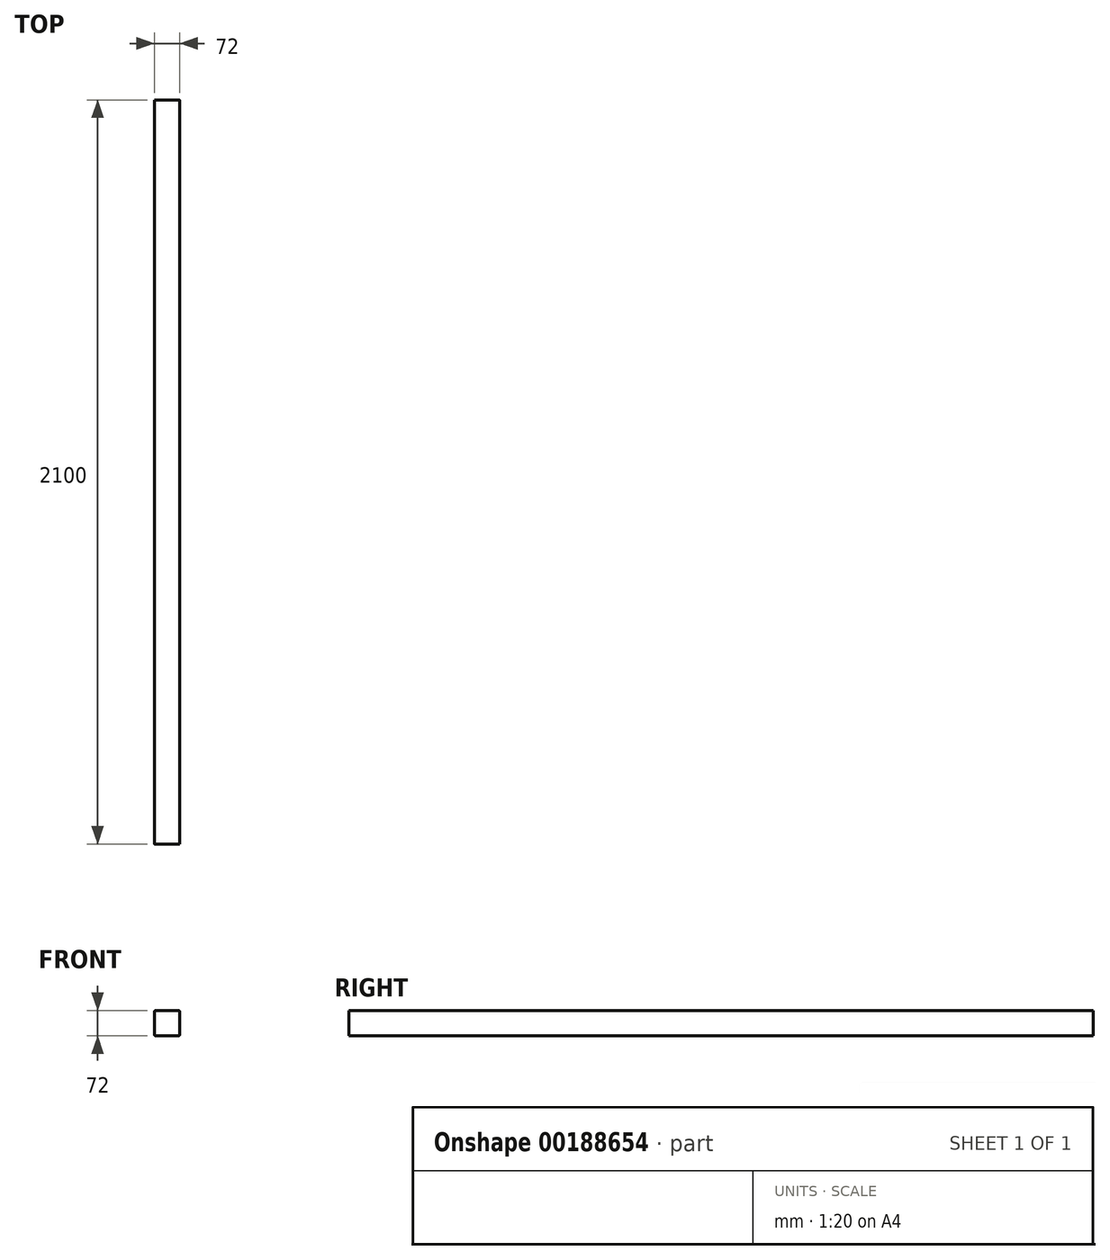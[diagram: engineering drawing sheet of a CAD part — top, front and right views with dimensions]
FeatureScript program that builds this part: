
annotation { "Feature Type Name" : "Feature", "Feature Type Description" : "" }
export const myFeature = defineFeature(function(context is Context, id is Id, definition is map)
    precondition{}
    {
        {
            var Q0;
            Q0=qCreatedBy(makeId("Front.planeOp"),FACE);
            var sketch = newSketch(context, id + "F0", { "sketchPlane" : qUnion([Q0])});
            skLineSegment(sketch, "E0.bottom", {"start": v(-31, 36) * mm, "end": v(31, 36) * mm});
            skLineSegment(sketch, "E0.top", {"start": v(-31, -36) * mm, "end": v(31, -36) * mm});
            skLineSegment(sketch, "E0.left", {"start": v(-36, 31) * mm, "end": v(-36, -31) * mm});
            skLineSegment(sketch, "E0.right", {"start": v(36, 31) * mm, "end": v(36, -31) * mm});
            skLineSegment(sketch, "E1", {"start": v(0, 53.32) * mm, "end": v(0, -69.02) * mm, "construction": true});
            skLineSegment(sketch, "E2", {"start": v(-62.16, 0) * mm, "end": v(68.96, 0) * mm, "construction": true});
            skPoint(sketch, "E3.visualSharp", {"position": v(-36, 36) * mm});
            skArc(sketch, "E3.filletArc", {"start": v(-31, 36) * mm, "mid": v(-34.54, 34.54) * mm, "end": v(-36, 31) * mm});
            skPoint(sketch, "E4.visualSharp", {"position": v(36, 36) * mm});
            skArc(sketch, "E4.filletArc", {"start": v(36, 31) * mm, "mid": v(34.54, 34.54) * mm, "end": v(31, 36) * mm});
            skPoint(sketch, "E5.visualSharp", {"position": v(36, -36) * mm});
            skArc(sketch, "E5.filletArc", {"start": v(31, -36) * mm, "mid": v(34.54, -34.54) * mm, "end": v(36, -31) * mm});
            skPoint(sketch, "E6.visualSharp", {"position": v(-36, -36) * mm});
            skArc(sketch, "E6.filletArc", {"start": v(-36, -31) * mm, "mid": v(-34.54, -34.54) * mm, "end": v(-31, -36) * mm});
            skSolve(sketch);
        }
        {
            var Q0;
            Q0 = qSketchRegion(id + "F0", true);
            extrude(context, id + "F1", {"entities" : qUnion([Q0]), "depth" : 2100 * mm});
        }
    });
